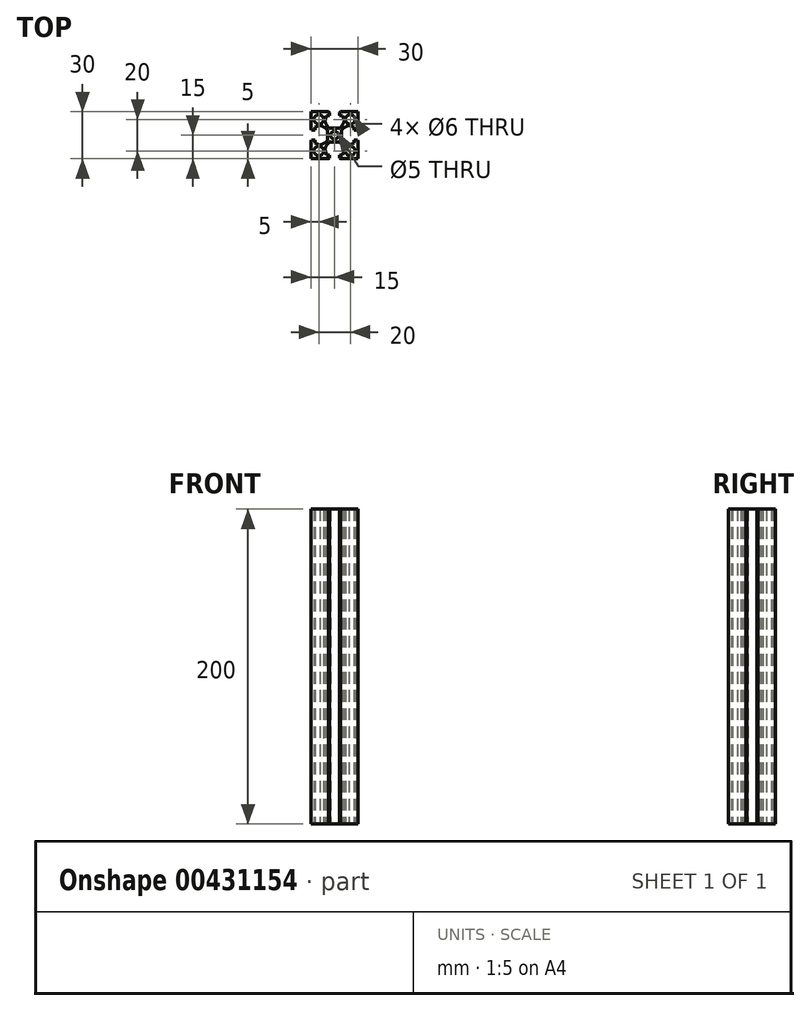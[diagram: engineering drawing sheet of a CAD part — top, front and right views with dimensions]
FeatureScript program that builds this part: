
annotation { "Feature Type Name" : "Feature", "Feature Type Description" : "" }
export const myFeature = defineFeature(function(context is Context, id is Id, definition is map)
    precondition{}
    {
        {
            var Q0;
            Q0=qCreatedBy(makeId("Top.planeOp"),FACE);
            var sketch = newSketch(context, id + "F0", { "sketchPlane" : qUnion([Q0])});
            skLineSegment(sketch, "E0.bottom", {"start": v(15, 15) * mm, "end": v(3.95, 15) * mm});
            skLineSegment(sketch, "E0.top", {"start": v(15, -15) * mm, "end": v(3.95, -15) * mm});
            skLineSegment(sketch, "E0.left", {"start": v(15, 15) * mm, "end": v(15, 3.95) * mm});
            skLineSegment(sketch, "E0.right", {"start": v(-15, 15) * mm, "end": v(-15, 3.95) * mm});
            skPoint(sketch, "E0.middle", {"position": v(0, 0) * mm});
            skLineSegment(sketch, "E1", {"start": v(0, 15) * mm, "end": v(0, -15) * mm, "construction": true});
            skLineSegment(sketch, "E2", {"start": v(-15, 0) * mm, "end": v(15, 0) * mm, "construction": true});
            skCircle(sketch, "E3", {"center": v(-10, 10) * mm, "radius": 3 * mm});
            skCircle(sketch, "E4", {"center": v(0, 0) * mm, "radius": 2.5 * mm});
            skLineSegment(sketch, "E5", {"start": v(0, 15) * mm, "end": v(0, 12.5) * mm, "construction": true});
            skLineSegment(sketch, "E6", {"start": v(-3.15, 14.5) * mm, "end": v(-3.15, 12.5) * mm});
            skLineSegment(sketch, "E7", {"start": v(-3.15, 12.5) * mm, "end": v(-5.1, 12.5) * mm});
            skLineSegment(sketch, "E8", {"start": v(0, 0) * mm, "end": v(-3.44, 0) * mm, "construction": true});
            skLineSegment(sketch, "E9", {"start": v(-5.1, 12.5) * mm, "end": v(-6.18, 9.16) * mm});
            skLineSegment(sketch, "E10", {"start": v(-3.44, 4.5) * mm, "end": v(0, 4.5) * mm});
            skLineSegment(sketch, "E11", {"start": v(3.36, 15) * mm, "end": v(3.36, 11.64) * mm, "construction": true});
            skArc(sketch, "E12", {"start": v(-3.44, 4.5) * mm, "mid": v(-5.13, 6.64) * mm, "end": v(-6.18, 9.16) * mm});
            skLineSegment(sketch, "E13", {"start": v(-3.95, 15) * mm, "end": v(-3.15, 14.5) * mm});
            skLineSegment(sketch, "E14.trimOffspring", {"start": v(-3.95, 15) * mm, "end": v(-5.1, 15) * mm, "construction": true});
            skLineSegment(sketch, "E15", {"start": v(-15, 15) * mm, "end": v(15, -15) * mm, "construction": true});
            skLineSegment(sketch, "E16", {"start": v(15, 15) * mm, "end": v(-15, -15) * mm, "construction": true});
            skArc(sketch, "E17.MirrorCS", {"start": v(-4.5, 3.43) * mm, "mid": v(-6.64, 5.13) * mm, "end": v(-9.16, 6.18) * mm});
            skLineSegment(sketch, "E18.MirrorCS", {"start": v(-4.5, 3.43) * mm, "end": v(-4.5, 0) * mm});
            skLineSegment(sketch, "E19.MirrorCS", {"start": v(-12.5, 5.1) * mm, "end": v(-9.16, 6.18) * mm});
            skLineSegment(sketch, "E20.MirrorCS", {"start": v(-12.5, 3.15) * mm, "end": v(-12.5, 5.1) * mm});
            skLineSegment(sketch, "E21.MirrorCS", {"start": v(-15, 3.95) * mm, "end": v(-14.5, 3.15) * mm});
            skLineSegment(sketch, "E22.MirrorCS", {"start": v(-14.5, 3.15) * mm, "end": v(-12.5, 3.15) * mm});
            skLineSegment(sketch, "E23.MirrorCS", {"start": v(-14.5, -3.15) * mm, "end": v(-12.5, -3.15) * mm});
            skLineSegment(sketch, "E24.MirrorCS", {"start": v(-15, -3.95) * mm, "end": v(-14.5, -3.15) * mm});
            skLineSegment(sketch, "E25.MirrorCS", {"start": v(-12.5, -3.15) * mm, "end": v(-12.5, -5.1) * mm});
            skLineSegment(sketch, "E26.MirrorCS", {"start": v(-12.5, -5.1) * mm, "end": v(-9.16, -6.18) * mm});
            skArc(sketch, "E27.MirrorCS", {"start": v(-4.5, -3.43) * mm, "mid": v(-6.64, -5.13) * mm, "end": v(-9.16, -6.18) * mm});
            skLineSegment(sketch, "E28.MirrorCS", {"start": v(-4.5, -3.43) * mm, "end": v(-4.5, 0) * mm});
            skLineSegment(sketch, "E29.MirrorCS", {"start": v(-3.44, -4.5) * mm, "end": v(0, -4.5) * mm});
            skArc(sketch, "E30.MirrorCS", {"start": v(-3.44, -4.5) * mm, "mid": v(-5.13, -6.64) * mm, "end": v(-6.18, -9.16) * mm});
            skLineSegment(sketch, "E31.MirrorCS", {"start": v(-5.1, -12.5) * mm, "end": v(-6.18, -9.16) * mm});
            skLineSegment(sketch, "E32.MirrorCS", {"start": v(-3.15, -12.5) * mm, "end": v(-5.1, -12.5) * mm});
            skLineSegment(sketch, "E33.MirrorCS", {"start": v(-3.95, -15) * mm, "end": v(-3.15, -14.5) * mm});
            skLineSegment(sketch, "E34.MirrorCS", {"start": v(-3.15, -14.5) * mm, "end": v(-3.15, -12.5) * mm});
            skLineSegment(sketch, "E35.MirrorCS", {"start": v(3.44, -4.5) * mm, "end": v(0, -4.5) * mm});
            skArc(sketch, "E36.MirrorCS", {"start": v(3.44, -4.5) * mm, "mid": v(5.13, -6.64) * mm, "end": v(6.18, -9.16) * mm});
            skLineSegment(sketch, "E37.MirrorCS", {"start": v(5.1, -12.5) * mm, "end": v(6.18, -9.16) * mm});
            skLineSegment(sketch, "E38.MirrorCS", {"start": v(3.15, -12.5) * mm, "end": v(5.1, -12.5) * mm});
            skLineSegment(sketch, "E39.MirrorCS", {"start": v(3.15, -14.5) * mm, "end": v(3.15, -12.5) * mm});
            skLineSegment(sketch, "E40.MirrorCS", {"start": v(3.95, -15) * mm, "end": v(3.15, -14.5) * mm});
            skArc(sketch, "E41.MirrorCS", {"start": v(4.5, -3.43) * mm, "mid": v(6.64, -5.13) * mm, "end": v(9.16, -6.18) * mm});
            skLineSegment(sketch, "E42.MirrorCS", {"start": v(4.5, 3.44) * mm, "end": v(4.5, 0) * mm});
            skLineSegment(sketch, "E43.MirrorCS", {"start": v(4.5, -3.43) * mm, "end": v(4.5, 0) * mm});
            skArc(sketch, "E44.MirrorCS", {"start": v(4.5, 3.44) * mm, "mid": v(6.64, 5.13) * mm, "end": v(9.16, 6.18) * mm});
            skLineSegment(sketch, "E45.MirrorCS", {"start": v(12.5, 5.1) * mm, "end": v(9.16, 6.18) * mm});
            skLineSegment(sketch, "E46.MirrorCS", {"start": v(12.5, -5.1) * mm, "end": v(9.16, -6.18) * mm});
            skLineSegment(sketch, "E47.MirrorCS", {"start": v(12.5, -3.15) * mm, "end": v(12.5, -5.1) * mm});
            skLineSegment(sketch, "E48.MirrorCS", {"start": v(14.5, -3.15) * mm, "end": v(12.5, -3.15) * mm});
            skLineSegment(sketch, "E49.MirrorCS", {"start": v(12.5, 3.15) * mm, "end": v(12.5, 5.1) * mm});
            skLineSegment(sketch, "E50.MirrorCS", {"start": v(14.5, 3.15) * mm, "end": v(12.5, 3.15) * mm});
            skLineSegment(sketch, "E51.MirrorCS", {"start": v(15, 3.95) * mm, "end": v(14.5, 3.15) * mm});
            skLineSegment(sketch, "E52.MirrorCS", {"start": v(15, -3.95) * mm, "end": v(14.5, -3.15) * mm});
            skLineSegment(sketch, "E53.MirrorCS", {"start": v(3.43, 4.5) * mm, "end": v(0, 4.5) * mm});
            skArc(sketch, "E54.MirrorCS", {"start": v(3.43, 4.5) * mm, "mid": v(5.13, 6.64) * mm, "end": v(6.18, 9.16) * mm});
            skLineSegment(sketch, "E55.MirrorCS", {"start": v(5.1, 12.5) * mm, "end": v(6.18, 9.16) * mm});
            skLineSegment(sketch, "E56.MirrorCS", {"start": v(3.15, 12.5) * mm, "end": v(5.1, 12.5) * mm});
            skLineSegment(sketch, "E57.MirrorCS", {"start": v(3.15, 14.5) * mm, "end": v(3.15, 12.5) * mm});
            skLineSegment(sketch, "E58.MirrorCS", {"start": v(3.95, 15) * mm, "end": v(3.15, 14.5) * mm});
            skCircle(sketch, "E59.MirrorC", {"center": v(10, 10) * mm, "radius": 3 * mm});
            skCircle(sketch, "E60.MirrorC", {"center": v(10, -10) * mm, "radius": 3 * mm});
            skCircle(sketch, "E61.MirrorC", {"center": v(-10, -10) * mm, "radius": 3 * mm});
            skLineSegment(sketch, "E62.trimOffspring", {"start": v(-15, -3.95) * mm, "end": v(-15, -15) * mm});
            skPoint(sketch, "E63.orphan", {"position": v(-15, 3.15) * mm});
            skPoint(sketch, "E64.orphan", {"position": v(-15, -3.15) * mm});
            skLineSegment(sketch, "E65.trimOffspring", {"start": v(-3.95, -15) * mm, "end": v(-15, -15) * mm});
            skPoint(sketch, "E66.orphan", {"position": v(-3.15, -15) * mm});
            skPoint(sketch, "E67.orphan", {"position": v(3.15, -15) * mm});
            skLineSegment(sketch, "E68.trimOffspring", {"start": v(15, -3.95) * mm, "end": v(15, -15) * mm});
            skPoint(sketch, "E69.orphan", {"position": v(15, 3.15) * mm});
            skPoint(sketch, "E70.orphan", {"position": v(15, -3.15) * mm});
            skPoint(sketch, "E71.trimOffspring.end.orphan", {"position": v(3.15, 15) * mm});
            skLineSegment(sketch, "E72.trimOffspring", {"start": v(-3.95, 15) * mm, "end": v(-15, 15) * mm});
            skPoint(sketch, "E73.trimOffspring.end.orphan", {"position": v(-3.15, 15) * mm});
            skSolve(sketch);
        }
        {
            var Q0;
            Q0=makeQuery(id+"F0.imprint","IMPRINT",FACE,{"disambiguationData":[TD([[makeQuery(id+"F0.imprint","IMPRINT",EDGE,{"derivedFrom":sQuery(id+"F0.wireOp",EDGE,"E0.bottom")}),1.0]])]});
            extrude(context, id + "F1", {"entities" : qUnion([Q0]), "endBound" : BoundingType.SYMMETRIC, "depth" : 200 * mm});
        }
    });
